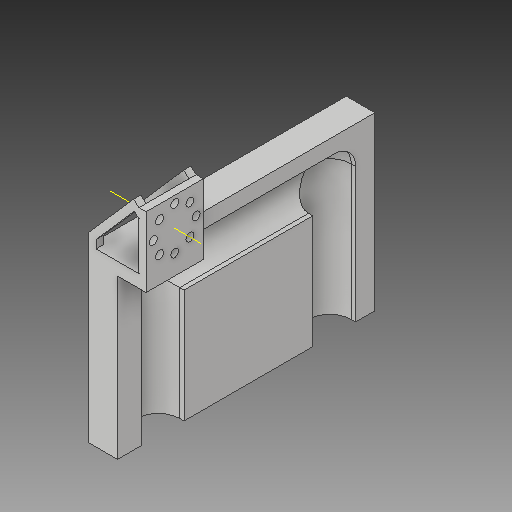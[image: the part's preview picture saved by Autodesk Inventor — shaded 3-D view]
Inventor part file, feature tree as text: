
AUTODESK INVENTOR PART (.ipt)
format: ipt  version: 2017 (Build 210142000, 142)  size: 239,616 bytes
history: native  units: in
note: dims shown in document units (in); Inventor stores cm internally (conversion verified against a paired STEP export)
features: sketch x7, extrude x6, projected_geometry x4, other x2, plane x1, mirror x1, pattern_circular x1, fillet x1
ambient origin geometry x8: Origin, YZ Plane, XZ Plane, XY Plane, X Axis, Y Axis, Z Axis, Center Point
bodies: Solid1 (feature_tree)
feature tree (23):
  other  "relicmold"
  extrude  "Extrusion1"  Depth=4.5in
  extrude  "Extrusion2"  Depth=1.0in
  extrude  "Extrusion3"  Depth=0.125in
  extrude  "Extrusion4"  Depth=0.125in
  plane  "Work Plane1"
  mirror  "Mirror1"
  extrude  "Extrusion5"  Depth=0.125in
  other  "Work Axis1"
  pattern_circular  "Circular Pattern1"  [2 undecoded]
  sketch  "Sketch6"  dims[d14=0.125in d15=0.0in]
  extrude  "Extrusion7"  Depth=1.0in
  fillet  "Fillet2"  Radius=0.5in
  sketch  "Sketch1"  dims[d0=3.0in d1=4.5in]
  sketch  "Sketch2"  dims[d2=0.5in d3=0.0in d4=1.0in]
  sketch  "Sketch3"  dims[d5=0.5in d6=0.0in d8=0.125in]
  projected_geometry  "Projected Loop1"
  sketch  "Sketch4"  dims[d9=1.0in d10=0.0in d11=0.125in]
  sketch  "Sketch5"  dims[d12=0.125in d13=0.125in]
  projected_geometry  "Projected Loop2"
  sketch  "Sketch7"  dims[d16=0.5in d17=1.0in d18=1.0in d19=0.5in d20=0.5in d21=0.14in d22=0.375in d23=0.125in d24=0.0in d25=3.1496in d26=360.0deg d28=0.75in d29=3.0in d30=0.75in d31=0.75in d32=3.75in d36=4.576in d37=0.413in d41=0.45in d42=0.0in d43=0.375in]
  projected_geometry  "Projected Loop3"
  projected_geometry  "Projected Loop4"
note: 2 required parameter values undecoded (feature->parameter linkage not recoverable at this tier; creation-order binding heuristic only, values carry confidence <= 0.55)
